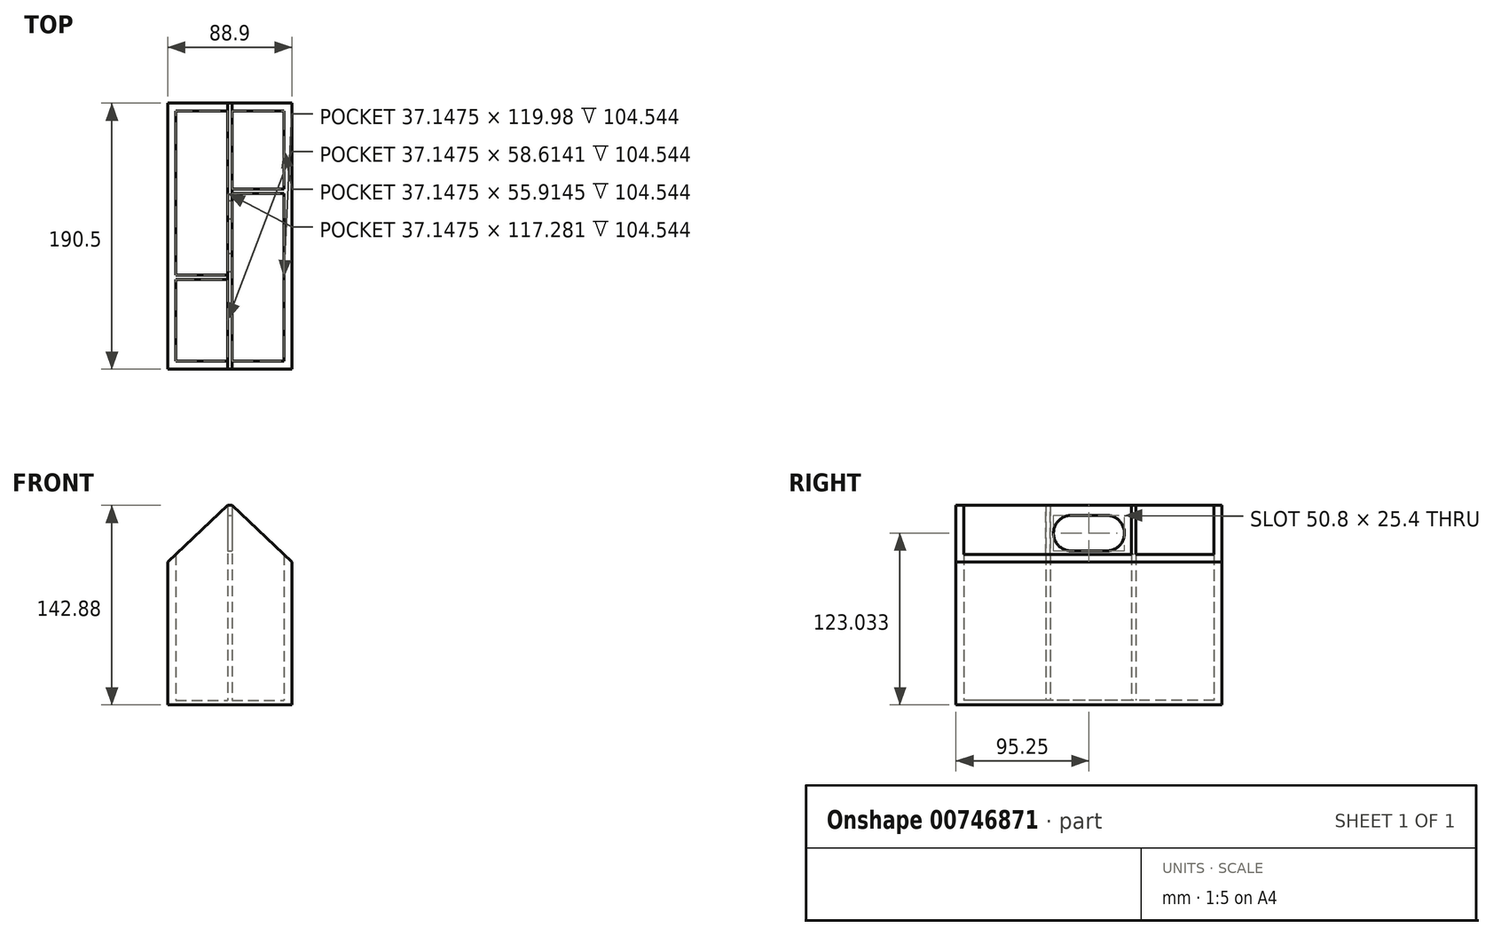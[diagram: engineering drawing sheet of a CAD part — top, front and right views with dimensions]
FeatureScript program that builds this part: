
annotation { "Feature Type Name" : "Feature", "Feature Type Description" : "" }
export const myFeature = defineFeature(function(context is Context, id is Id, definition is map)
    precondition{}
    {
        {
            var Q0;
            Q0=qCreatedBy(makeId("Top.planeOp"),FACE);
            var sketch = newSketch(context, id + "F0", { "sketchPlane" : qUnion([Q0])});
            skLineSegment(sketch, "E0.bottom", {"start": v(-44.45, 95.25) * mm, "end": v(44.45, 95.25) * mm});
            skLineSegment(sketch, "E0.top", {"start": v(-44.45, -95.25) * mm, "end": v(44.45, -95.25) * mm});
            skLineSegment(sketch, "E0.left", {"start": v(-44.45, 95.25) * mm, "end": v(-44.45, -95.25) * mm});
            skLineSegment(sketch, "E0.right", {"start": v(44.45, 95.25) * mm, "end": v(44.45, -95.25) * mm});
            skLineSegment(sketch, "E1.0", {"start": v(41.28, 92.08) * mm, "end": v(41.27, -92.08) * mm});
            skLineSegment(sketch, "E1.1", {"start": v(-41.28, 92.08) * mm, "end": v(41.28, 92.08) * mm});
            skLineSegment(sketch, "E1.2", {"start": v(-41.27, 92.08) * mm, "end": v(-41.27, -92.08) * mm});
            skLineSegment(sketch, "E1.3", {"start": v(-41.28, -92.08) * mm, "end": v(41.28, -92.08) * mm});
            skLineSegment(sketch, "E2", {"start": v(0, 95.25) * mm, "end": v(0, 0) * mm, "construction": true});
            skLineSegment(sketch, "E3", {"start": v(0, 0) * mm, "end": v(-41.27, 0) * mm, "construction": true});
            skSolve(sketch);
        }
        {
            var Q0;
            Q0=makeQuery(id+"F0.imprint","IMPRINT",FACE,{"disambiguationData":[TD([[makeQuery(id+"F0.imprint","IMPRINT",EDGE,{"derivedFrom":sQuery(id+"F0.wireOp",EDGE,"E1.0")}),-1.0]])]});
            var Q1;
            Q1=makeQuery(id+"F0.imprint","IMPRINT",FACE,{"disambiguationData":[TD([[makeQuery(id+"F0.imprint","IMPRINT",EDGE,{"derivedFrom":sQuery(id+"F0.wireOp",EDGE,"E0.bottom")}),-1.0]])]});
            extrude(context, id + "F1", {"entities" : qUnion([Q0, Q1]), "depth" : 3.17 * mm, "offsetDistance" : 25.4 * mm});
        }
        {
            var Q0;
            Q0=makeQuery(id+"F1.opExtrude","CAP_FACE",FACE,{"disambiguationData":[OSD([sQuery(id+"F0.wireOp",EDGE,"E0.bottom"),sQuery(id+"F0.wireOp",EDGE,"E0.top"),sQuery(id+"F0.wireOp",EDGE,"E0.left"),sQuery(id+"F0.wireOp",EDGE,"E0.right")])],"isStart":false});
            var sketch = newSketch(context, id + "F2", { "sketchPlane" : qUnion([Q0])});
            skLineSegment(sketch, "E4.0", {"start": v(-38.74, -89.54) * mm, "end": v(38.73, -89.54) * mm});
            skLineSegment(sketch, "E4.1", {"start": v(-38.73, 89.53) * mm, "end": v(-38.74, -89.54) * mm});
            skLineSegment(sketch, "E4.2", {"start": v(-38.73, 89.53) * mm, "end": v(38.73, 89.53) * mm});
            skLineSegment(sketch, "E4.3", {"start": v(38.73, 89.53) * mm, "end": v(38.73, -89.54) * mm});
            skLineSegment(sketch, "E5.0", {"start": v(-38.74, -30.92) * mm, "end": v(1.59, -30.92) * mm});
            skLineSegment(sketch, "E6.0", {"start": v(-38.74, -27.75) * mm, "end": v(1.59, -27.75) * mm});
            skLineSegment(sketch, "E7.0", {"start": v(-1.59, 30.45) * mm, "end": v(38.73, 30.45) * mm});
            skLineSegment(sketch, "E8.0", {"start": v(-1.59, 33.62) * mm, "end": v(38.73, 33.62) * mm});
            skLineSegment(sketch, "E9", {"start": v(0, 89.53) * mm, "end": v(0, -89.54) * mm, "construction": true});
            skLineSegment(sketch, "E10.0", {"start": v(-1.59, 89.53) * mm, "end": v(-1.59, -89.54) * mm});
            skLineSegment(sketch, "E11", {"start": v(1.59, 89.53) * mm, "end": v(1.59, -89.54) * mm});
            skSolve(sketch);
        }
        {
            var Q0;
            Q0=makeQuery(id+"F2.imprint","IMPRINT",FACE,{"disambiguationData":[TD([[makeQuery(id+"F2.imprint","IMPRINT",EDGE,{"derivedFrom":sQuery(id+"F2.wireOp",EDGE,"E4.0")}),-1.0]])]});
            var Q1;
            {var subQ0=sQuery(id+"F2.wireOp",EDGE,"E7.0");Q1=makeQuery(id+"F2.imprint","IMPRINT",FACE,{"disambiguationData":[TD([[makeQuery(id+"F2.imprint","IMPRINT",EDGE,{"derivedFrom":subQ0}),1.0]])]});}
            var Q2;
            {var subQ0=sQuery(id+"F2.wireOp",EDGE,"E5.0");Q2=makeQuery(id+"F2.imprint","IMPRINT",FACE,{"disambiguationData":[TD([[makeQuery(id+"F2.imprint","IMPRINT",EDGE,{"derivedFrom":subQ0}),1.0]])]});}
            var Q3;
            {var subQ0=sQuery(id+"F2.wireOp",EDGE,"E10.0");var subQ1=sQuery(id+"F2.wireOp",EDGE,"E6.0");var subQ2=makeQuery(id+"F2.imprint","INTERSECT",VERTEX,{"derivedFrom":[subQ1,subQ0]});Q3=makeQuery(id+"F2.imprint","IMPRINT",FACE,{"disambiguationData":[TD([[makeQuery(id+"F2.imprint","IMPRINT",EDGE,{"disambiguationData":[TD([[subQ2,-1.0]])],"derivedFrom":subQ1}),1.0]])]});}
            var Q4;
            {var subQ0=sQuery(id+"F2.wireOp",EDGE,"E10.0");var subQ1=sQuery(id+"F2.wireOp",EDGE,"E4.2");var subQ2=makeQuery(id+"F2.imprint","INTERSECT",VERTEX,{"derivedFrom":[subQ1,subQ0]});Q4=makeQuery(id+"F2.imprint","IMPRINT",FACE,{"disambiguationData":[TD([[makeQuery(id+"F2.imprint","IMPRINT",EDGE,{"disambiguationData":[TD([[subQ2,-1.0]])],"derivedFrom":subQ1}),-1.0]])]});}
            var Q5;
            {var subQ0=sQuery(id+"F2.wireOp",EDGE,"E10.0");var subQ1=sQuery(id+"F2.wireOp",EDGE,"E4.0");var subQ2=makeQuery(id+"F2.imprint","INTERSECT",VERTEX,{"derivedFrom":[subQ1,subQ0]});Q5=makeQuery(id+"F2.imprint","IMPRINT",FACE,{"disambiguationData":[TD([[makeQuery(id+"F2.imprint","IMPRINT",EDGE,{"disambiguationData":[TD([[subQ2,-1.0]])],"derivedFrom":subQ1}),1.0]])]});}
            extrude(context, id + "F3", {"entities" : qUnion([Q0, Q1, Q2, Q3, Q4, Q5]), "operationType" : NewBodyOperationType.ADD, "depth" : 139.7 * mm, "offsetDistance" : 25.4 * mm});
        }
        {
            var Q0;
            Q0=makeQuery(id+"F3.opExtrude","CAP_FACE",FACE,{"disambiguationData":[OSD([sQuery(id+"F0.wireOp",EDGE,"E0.bottom"),sQuery(id+"F0.wireOp",EDGE,"E0.top"),sQuery(id+"F0.wireOp",EDGE,"E0.left"),sQuery(id+"F0.wireOp",EDGE,"E0.right"),sQuery(id+"F2.wireOp",EDGE,"E4.0"),sQuery(id+"F2.wireOp",EDGE,"E4.1"),sQuery(id+"F2.wireOp",EDGE,"E4.2"),sQuery(id+"F2.wireOp",EDGE,"E4.3"),sQuery(id+"F2.wireOp",EDGE,"E5.0"),sQuery(id+"F2.wireOp",EDGE,"E6.0"),sQuery(id+"F2.wireOp",EDGE,"E7.0"),sQuery(id+"F2.wireOp",EDGE,"E8.0"),sQuery(id+"F2.wireOp",EDGE,"E10.0"),sQuery(id+"F2.wireOp",EDGE,"E11")])],"isStart":false});
            var sketch = newSketch(context, id + "F4", { "sketchPlane" : qUnion([Q0])});
            skLineSegment(sketch, "E12", {"start": v(-1.59, -89.54) * mm, "end": v(-1.59, -95.25) * mm, "construction": true});
            skLineSegment(sketch, "E13", {"start": v(1.59, -89.54) * mm, "end": v(1.59, -95.25) * mm, "construction": true});
            skLineSegment(sketch, "E14", {"start": v(0, -95.25) * mm, "end": v(0, 95.25) * mm, "construction": true});
            skLineSegment(sketch, "E15", {"start": v(0, 0) * mm, "end": v(1.59, 0) * mm, "construction": true});
            skLineSegment(sketch, "E16", {"start": v(1.59, 0) * mm, "end": v(-1.59, 0) * mm, "construction": true});
            skSolve(sketch);
        }
        {
            var Q0;
            {var subQ0=sQuery(id+"F0.wireOp",EDGE,"E0.top");Q0=makeQuery(id+"F3.boolean.opBoolean","MERGE",FACE,{"derivedFrom":[makeQuery(id+"F1.opExtrude","SWEPT_FACE",FACE,{"disambiguationData":[OSD([subQ0])]}),makeQuery(id+"F3.opExtrude","SWEPT_FACE",FACE,{"disambiguationData":[OSD([subQ0])]})]});}
            var sketch = newSketch(context, id + "F5", { "sketchPlane" : qUnion([Q0])});
            skLineSegment(sketch, "E17", {"start": v(0, 142.88) * mm, "end": v(0, 0) * mm, "construction": true});
            skLineSegment(sketch, "E18", {"start": v(-1.59, 142.88) * mm, "end": v(-44.45, 102.31) * mm});
            skLineSegment(sketch, "E19.MirrorCS", {"start": v(1.59, 142.88) * mm, "end": v(44.45, 102.31) * mm});
            skSolve(sketch);
        }
        {
            var Q0;
            {var subQ0=sQuery(id+"F5.wireOp",EDGE,"uBFHS7lY-nYPi-gax1-MjNy-eMbcI1F449uY");Q0=makeQuery(id+"F5.imprint","IMPRINT",FACE,{"disambiguationData":[TD([[makeQuery(id+"F5.imprint","IMPRINT",EDGE,{"derivedFrom":subQ0}),-1.0]])]});}
            var Q1;
            {var subQ0=sQuery(id+"F5.wireOp",EDGE,"7cbcd53b-bc9a-4f41-95ed-080ec99d8f570.MirrorCS");Q1=makeQuery(id+"F5.imprint","IMPRINT",FACE,{"disambiguationData":[TD([[makeQuery(id+"F5.imprint","IMPRINT",EDGE,{"derivedFrom":subQ0}),1.0]])]});}
            var Q2;
            {var subQ0=sQuery(id+"F5.wireOp",EDGE,"E18");Q2=makeQuery(id+"F5.imprint","IMPRINT",FACE,{"disambiguationData":[TD([[makeQuery(id+"F5.imprint","IMPRINT",EDGE,{"derivedFrom":subQ0}),-1.0]])]});}
            var Q3;
            {var subQ0=sQuery(id+"F5.wireOp",EDGE,"E19.MirrorCS");Q3=makeQuery(id+"F5.imprint","IMPRINT",FACE,{"disambiguationData":[TD([[makeQuery(id+"F5.imprint","IMPRINT",EDGE,{"derivedFrom":subQ0}),1.0]])]});}
            extrude(context, id + "F6", {"entities" : qUnion([Q0, Q1, Q2, Q3]), "operationType" : NewBodyOperationType.REMOVE, "oppositeDirection" : true, "depth" : 190.5 * mm, "offsetDistance" : 25.4 * mm});
        }
        {
            var Q0;
            {var subQ0=sQuery(id+"F2.wireOp",EDGE,"E11");var subQ1=makeQuery(id+"F2.imprint","INTERSECT",VERTEX,{"derivedFrom":[sQuery(id+"F2.wireOp",EDGE,"E5.0"),subQ0]});var subQ2=makeQuery(id+"F2.imprint","INTERSECT",VERTEX,{"derivedFrom":[sQuery(id+"F2.wireOp",EDGE,"E6.0"),subQ0]});Q0=makeQuery(id+"F3.opExtrude","SWEPT_FACE",FACE,{"disambiguationData":[OSD([subQ0]),TDD([makeQuery(id+"F2.imprint","IMPRINT",EDGE,{"disambiguationData":[TD([[subQ2,1.0]])],"derivedFrom":subQ0}),makeQuery(id+"F2.imprint","IMPRINT",EDGE,{"disambiguationData":[TD([[subQ1,1.0]])],"derivedFrom":subQ0}),makeQuery(id+"F2.imprint","IMPRINT",EDGE,{"disambiguationData":[TD([[subQ1,-1.0]])],"derivedFrom":subQ0})])]});}
            var sketch = newSketch(context, id + "F7", { "sketchPlane" : qUnion([Q0])});
            skLineSegment(sketch, "E20", {"start": v(0, 142.88) * mm, "end": v(0, 116.24) * mm, "construction": true});
            skLineSegment(sketch, "E21", {"start": v(0, 135.73) * mm, "end": v(12.7, 135.73) * mm});
            skLineSegment(sketch, "E22.0", {"start": v(0, 110.33) * mm, "end": v(12.4, 110.33) * mm});
            skArc(sketch, "E23", {"start": v(12.7, 135.73) * mm, "mid": v(25.4, 122.89) * mm, "end": v(12.4, 110.33) * mm});
            skLineSegment(sketch, "E24.MirrorCS", {"start": v(0, 135.73) * mm, "end": v(-12.7, 135.73) * mm});
            skLineSegment(sketch, "E25.MirrorCS", {"start": v(0, 110.33) * mm, "end": v(-12.4, 110.33) * mm});
            skArc(sketch, "E26.MirrorCS", {"start": v(-12.7, 135.73) * mm, "mid": v(-25.4, 122.89) * mm, "end": v(-12.4, 110.33) * mm});
            skSolve(sketch);
        }
        {
            var Q0;
            Q0=makeQuery(id+"F7.imprint","IMPRINT",FACE,{"disambiguationData":[TD([[makeQuery(id+"F7.imprint","IMPRINT",EDGE,{"derivedFrom":sQuery(id+"F7.wireOp",EDGE,"E21")}),-1.0]])]});
            extrude(context, id + "F8", {"entities" : qUnion([Q0]), "operationType" : NewBodyOperationType.REMOVE, "oppositeDirection" : true, "depth" : 25.4 * mm, "offsetDistance" : 25.4 * mm});
        }
    });
